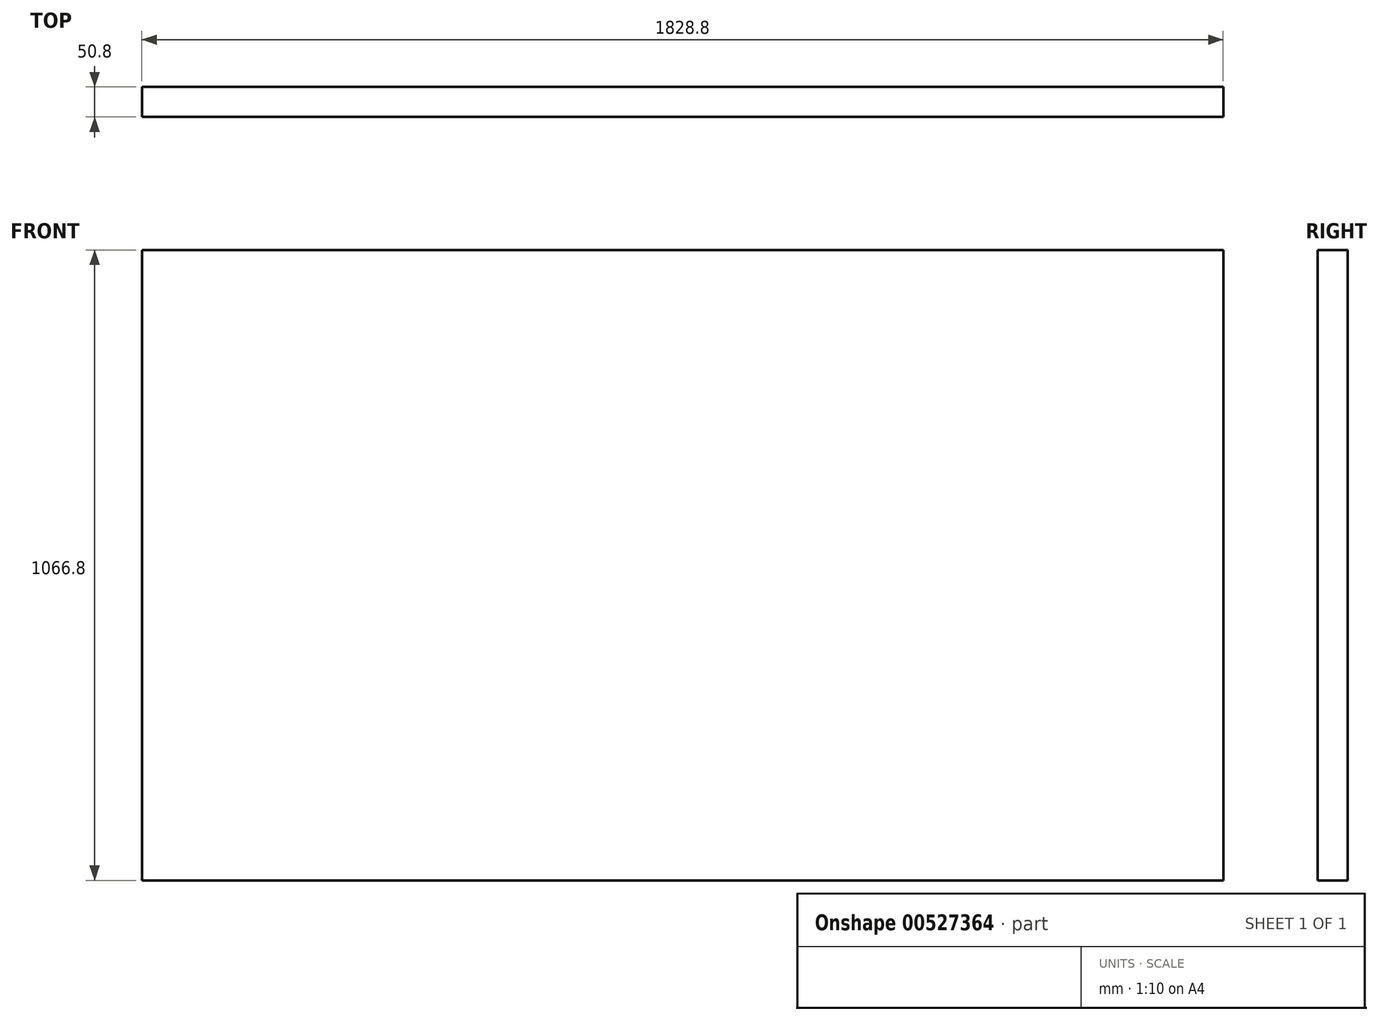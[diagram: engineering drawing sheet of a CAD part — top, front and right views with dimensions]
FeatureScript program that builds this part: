
annotation { "Feature Type Name" : "Feature", "Feature Type Description" : "" }
export const myFeature = defineFeature(function(context is Context, id is Id, definition is map)
    precondition{}
    {
        {
            var Q0;
            Q0=qCreatedBy(makeId("Front.planeOp"),FACE);
            var sketch = newSketch(context, id + "F0", { "sketchPlane" : qUnion([Q0])});
            skLineSegment(sketch, "E0.bottom", {"start": v(-1161.28, 510.38) * mm, "end": v(667.52, 510.38) * mm});
            skLineSegment(sketch, "E0.top", {"start": v(-1161.28, -556.42) * mm, "end": v(667.52, -556.42) * mm});
            skLineSegment(sketch, "E0.left", {"start": v(-1161.28, 510.38) * mm, "end": v(-1161.28, -556.42) * mm});
            skLineSegment(sketch, "E0.right", {"start": v(667.52, 510.38) * mm, "end": v(667.52, -556.42) * mm});
            skSolve(sketch);
        }
        {
            var Q0;
            Q0=makeQuery(id+"F0.imprint","IMPRINT",FACE,{"disambiguationData":[TD([[makeQuery(id+"F0.imprint","IMPRINT",EDGE,{"derivedFrom":sQuery(id+"F0.wireOp",EDGE,"E0.bottom")}),-1.0]])]});
            extrude(context, id + "F1", {"entities" : qUnion([Q0]), "depth" : 50.8 * mm, "offsetDistance" : 25.4 * mm});
        }
    });
